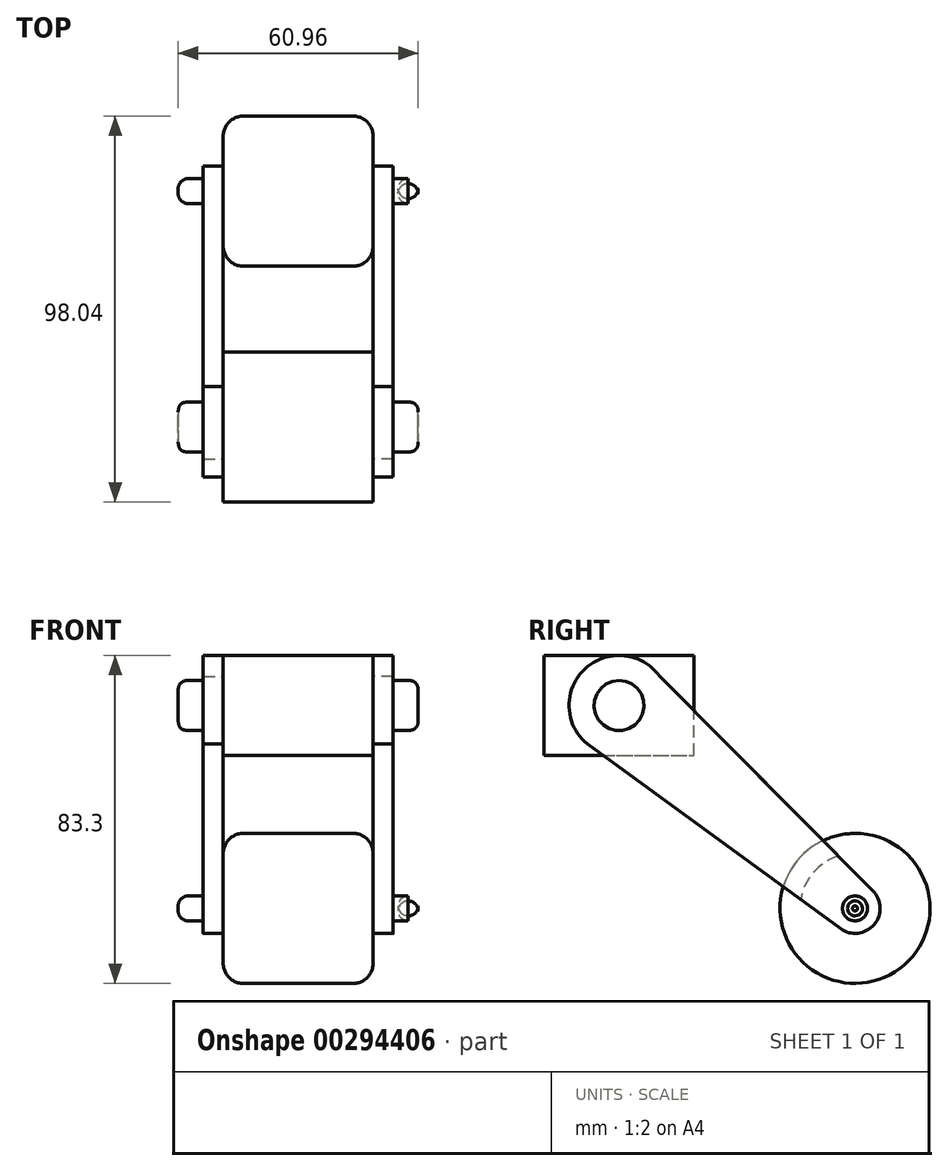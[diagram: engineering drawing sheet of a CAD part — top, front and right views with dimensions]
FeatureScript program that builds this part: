
annotation { "Feature Type Name" : "Feature", "Feature Type Description" : "" }
export const myFeature = defineFeature(function(context is Context, id is Id, definition is map)
    precondition{}
    {
        {
            var Q0;
            Q0=qCreatedBy(makeId("Right.planeOp"),FACE);
            var sketch = newSketch(context, id + "F0", { "sketchPlane" : qUnion([Q0])});
            skLineSegment(sketch, "E0.bottom", {"start": v(-59, 38.85) * mm, "end": v(-20.9, 38.85) * mm});
            skLineSegment(sketch, "E0.top", {"start": v(-59, 64.25) * mm, "end": v(-20.9, 64.25) * mm});
            skLineSegment(sketch, "E0.left", {"start": v(-59, 38.85) * mm, "end": v(-59, 64.25) * mm});
            skLineSegment(sketch, "E0.right", {"start": v(-20.9, 38.85) * mm, "end": v(-20.9, 64.25) * mm});
            skSolve(sketch);
        }
        {
            var Q0;
            Q0=makeQuery(id+"F0.imprint","IMPRINT",FACE,{"disambiguationData":[TD([[makeQuery(id+"F0.imprint","IMPRINT",EDGE,{"derivedFrom":sQuery(id+"F0.wireOp",EDGE,"E0.bottom")}),1.0]])]});
            extrude(context, id + "F1", {"entities" : qUnion([Q0]), "depth" : 19.05 * mm, "hasSecondDirection" : true, "secondDirectionOppositeDirection" : true, "secondDirectionDepth" : 19.05 * mm});
        }
        {
            var Q0;
            Q0=makeQuery(id+"F1.opExtrude","CAP_FACE",FACE,{"disambiguationData":[OSD([sQuery(id+"F0.wireOp",EDGE,"E0.bottom"),sQuery(id+"F0.wireOp",EDGE,"E0.top"),sQuery(id+"F0.wireOp",EDGE,"E0.left"),sQuery(id+"F0.wireOp",EDGE,"E0.right")])],"isStart":false});
            var sketch = newSketch(context, id + "F2", { "sketchPlane" : qUnion([Q0])});
            skArc(sketch, "E1", {"start": v(-29.6, 58.92) * mm, "mid": v(-48.61, 60.84) * mm, "end": v(-48.03, 41.75) * mm});
            skPoint(sketch, "E1.centerSnap0", {"position": v(-59, 51.55) * mm});
            skPoint(sketch, "E1.centerSnap1", {"position": v(-39.95, 38.85) * mm});
            skArc(sketch, "E2", {"start": v(16.24, -5.14) * mm, "mid": v(24.82, -4.14) * mm, "end": v(24.5, 4.48) * mm});
            skLineSegment(sketch, "E3", {"start": v(-29.6, 58.92) * mm, "end": v(24.5, 4.48) * mm});
            skLineSegment(sketch, "E4", {"start": v(-48.03, 41.75) * mm, "end": v(16.24, -5.14) * mm});
            skCircle(sketch, "E5", {"center": v(20, 0) * mm, "radius": 3.18 * mm});
            skSolve(sketch);
        }
        {
            var Q0;
            Q0 = qSketchRegion(id + "F2", true);
            extrude(context, id + "F3", {"entities" : qUnion([Q0]), "depth" : 5.08 * mm});
        }
        {
            var Q0;
            Q0=makeQuery(id+"F3.opExtrude","CAP_FACE",FACE,{"disambiguationData":[OSD([sQuery(id+"F2.wireOp",EDGE,"E1"),sQuery(id+"F2.wireOp",EDGE,"E2"),sQuery(id+"F2.wireOp",EDGE,"E3"),sQuery(id+"F2.wireOp",EDGE,"E4")])],"isStart":true});
            cPlane(context, id + "F4", {"entities" : qUnion([Q0]), "cplaneType" : CPlaneType.OFFSET, "offset" : 19.05 * mm, "width" : 152.4 * mm, "height" : 152.4 * mm});
        }
        {
            var Q0;
            Q0=makeQuery(id+"F3.opExtrude","SWEPT_BODY",BODY,{"disambiguationData":[OSD([sQuery(id+"F2.wireOp",EDGE,"E1"),sQuery(id+"F2.wireOp",EDGE,"E2"),sQuery(id+"F2.wireOp",EDGE,"E3"),sQuery(id+"F2.wireOp",EDGE,"E4")])]});
            var Q1;
            Q1=qCreatedBy(id+"F4.planeOp",FACE);
            mirror(context, id + "F5", {"entities" : qUnion([Q0]), "mirrorPlane" : qUnion([Q1])});
        }
        {
            var Q0;
            Q0=makeQuery(id+"F3.opExtrude","CAP_FACE",FACE,{"disambiguationData":[OSD([sQuery(id+"F2.wireOp",EDGE,"E1"),sQuery(id+"F2.wireOp",EDGE,"E2"),sQuery(id+"F2.wireOp",EDGE,"E3"),sQuery(id+"F2.wireOp",EDGE,"E4")])],"isStart":true});
            var sketch = newSketch(context, id + "F6", { "sketchPlane" : qUnion([Q0])});
            skCircle(sketch, "E6", {"center": v(-20, 0) * mm, "radius": 19.05 * mm});
            skCircle(sketch, "E7", {"center": v(-20, 0) * mm, "radius": 3.18 * mm});
            skSolve(sketch);
        }
        {
            var Q0;
            Q0 = qSketchRegion(id + "F6", true);
            extrude(context, id + "F7", {"entities" : qUnion([Q0]), "depth" : 38.1 * mm});
        }
        {
            var Q0;
            Q0=makeQuery(id+"F5.opPattern","COPY",FACE,{"derivedFrom":makeQuery(id+"F3.opExtrude","CAP_FACE",FACE,{"disambiguationData":[OSD([sQuery(id+"F2.wireOp",EDGE,"E1"),sQuery(id+"F2.wireOp",EDGE,"E2"),sQuery(id+"F2.wireOp",EDGE,"E3"),sQuery(id+"F2.wireOp",EDGE,"E4")])],"isStart":false}),"instanceName":"1"});
            var sketch = newSketch(context, id + "F8", { "sketchPlane" : qUnion([Q0])});
            skCircle(sketch, "E8", {"center": v(39.95, 51.55) * mm, "radius": 6.35 * mm});
            skSolve(sketch);
        }
        {
            var Q0;
            Q0 = qSketchRegion(id + "F8", true);
            extrude(context, id + "F9", {"entities" : qUnion([Q0]), "depth" : 6.35 * mm});
        }
        {
            var Q0;
            Q0=makeQuery(id+"F9.opExtrude","CAP_FACE",FACE,{"disambiguationData":[OSD([sQuery(id+"F8.wireOp",EDGE,"E8")])],"isStart":false});
            fillet(context, id + "F10", {"entities" : qUnion([Q0]), "radius" : 2.54 * mm, "tangentPropagation" : true, "rho" : 0.5, "crossSection" : FilletCrossSection.CONIC, "allowEdgeOverflow" : false});
        }
        {
            var Q0;
            Q0=makeQuery(id+"F9.opExtrude","SWEPT_BODY",BODY,{"disambiguationData":[OSD([sQuery(id+"F8.wireOp",EDGE,"E8")])]});
            var Q1;
            Q1=qCreatedBy(id+"F4.planeOp",FACE);
            mirror(context, id + "F11", {"entities" : qUnion([Q0]), "mirrorPlane" : qUnion([Q1])});
        }
        {
            var Q0;
            Q0=makeQuery(id+"F7.opExtrude","CAP_EDGE",EDGE,{"disambiguationData":[OSD([sQuery(id+"F6.wireOp",EDGE,"E6")])],"isStart":true});
            fillet(context, id + "F12", {"entities" : qUnion([Q0]), "radius" : 5.08 * mm, "tangentPropagation" : true, "allowEdgeOverflow" : false});
        }
        {
            var Q0;
            Q0=makeQuery(id+"F7.opExtrude","CAP_EDGE",EDGE,{"disambiguationData":[OSD([sQuery(id+"F6.wireOp",EDGE,"E6")])],"isStart":false});
            fillet(context, id + "F13", {"entities" : qUnion([Q0]), "radius" : 5.08 * mm, "tangentPropagation" : true, "allowEdgeOverflow" : false});
        }
        {
            var Q0;
            Q0=makeQuery(id+"F5.opPattern","COPY",FACE,{"derivedFrom":makeQuery(id+"F3.opExtrude","CAP_FACE",FACE,{"disambiguationData":[OSD([sQuery(id+"F2.wireOp",EDGE,"E1"),sQuery(id+"F2.wireOp",EDGE,"E2"),sQuery(id+"F2.wireOp",EDGE,"E3"),sQuery(id+"F2.wireOp",EDGE,"E4"),sQuery(id+"F2.wireOp",EDGE,"E5")])],"isStart":false}),"instanceName":"1"});
            var sketch = newSketch(context, id + "F14", { "sketchPlane" : qUnion([Q0])});
            skCircle(sketch, "E9", {"center": v(-20, 0) * mm, "radius": 3.18 * mm});
            skSolve(sketch);
        }
        {
            var Q0;
            Q0 = qSketchRegion(id + "F14", true);
            extrude(context, id + "F15", {"entities" : qUnion([Q0]), "operationType" : NewBodyOperationType.ADD, "depth" : 6.35 * mm, "hasSecondDirection" : true, "secondDirectionOppositeDirection" : true, "secondDirectionDepth" : 54.6 * mm});
        }
        {
            var Q0;
            Q0=makeQuery(id+"F15.opExtrude","CAP_EDGE",EDGE,{"disambiguationData":[OSD([sQuery(id+"F14.wireOp",EDGE,"E9")])],"isStart":true});
            fillet(context, id + "F16", {"entities" : qUnion([Q0]), "radius" : 2.54 * mm, "tangentPropagation" : true, "allowEdgeOverflow" : false});
        }
        {
            var Q0;
            Q0=makeQuery(id+"F15.opExtrude","CAP_EDGE",EDGE,{"disambiguationData":[OSD([sQuery(id+"F14.wireOp",EDGE,"E9")])],"isStart":false});
            fillet(context, id + "F17", {"entities" : qUnion([Q0]), "radius" : 2.54 * mm, "tangentPropagation" : true, "allowEdgeOverflow" : false});
        }
    });
